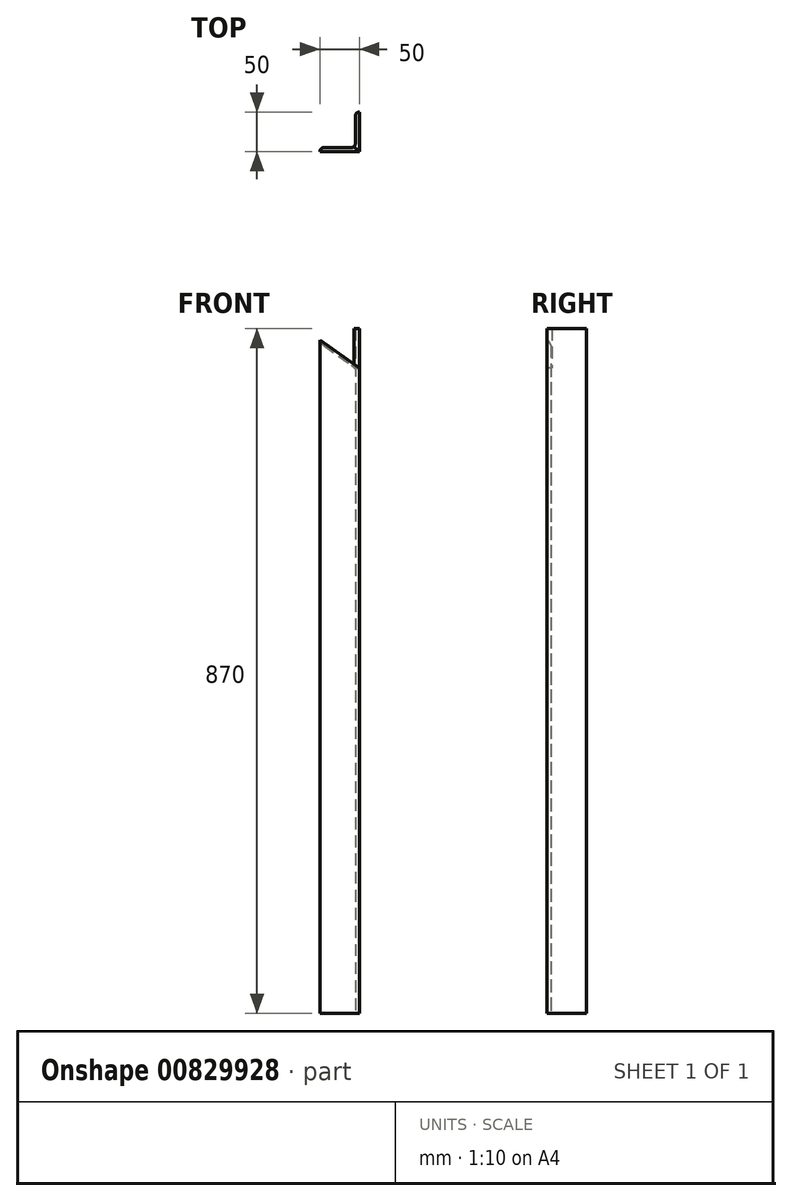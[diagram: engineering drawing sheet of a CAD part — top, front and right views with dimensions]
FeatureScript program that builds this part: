
annotation { "Feature Type Name" : "Feature", "Feature Type Description" : "" }
export const myFeature = defineFeature(function(context is Context, id is Id, definition is map)
    precondition{}
    {
        {
            var Q0;
            Q0=qCreatedBy(makeId("Top.planeOp"),FACE);
            var sketch = newSketch(context, id + "F0", { "sketchPlane" : qUnion([Q0])});
            skLineSegment(sketch, "E0", {"start": v(0, 0) * mm, "end": v(0, 50) * mm});
            skLineSegment(sketch, "E1", {"start": v(0, 0) * mm, "end": v(-50, 0) * mm});
            skLineSegment(sketch, "E2", {"start": v(-50, 0) * mm, "end": v(-50, 0) * mm});
            skLineSegment(sketch, "E3", {"start": v(-45, 5) * mm, "end": v(-10, 5) * mm});
            skLineSegment(sketch, "E4", {"start": v(-5, 10) * mm, "end": v(-5, 45) * mm});
            skLineSegment(sketch, "E5", {"start": v(0, 50) * mm, "end": v(0, 50) * mm});
            skPoint(sketch, "E6.visualSharp", {"position": v(-50, 5) * mm});
            skArc(sketch, "E6.filletArc", {"start": v(-45, 5) * mm, "mid": v(-48.54, 3.54) * mm, "end": v(-50, 0) * mm});
            skPoint(sketch, "E7.visualSharp", {"position": v(-5, 50) * mm});
            skArc(sketch, "E7.filletArc", {"start": v(0, 50) * mm, "mid": v(-3.54, 48.54) * mm, "end": v(-5, 45) * mm});
            skPoint(sketch, "E8.visualSharp", {"position": v(-5, 5) * mm});
            skArc(sketch, "E8.filletArc", {"start": v(-10, 5) * mm, "mid": v(-6.46, 6.46) * mm, "end": v(-5, 10) * mm});
            skSolve(sketch);
        }
        {
            var Q0;
            Q0=makeQuery(id+"F0.imprint","IMPRINT",FACE,{"disambiguationData":[TD([[makeQuery(id+"F0.imprint","IMPRINT",EDGE,{"derivedFrom":sQuery(id+"F0.wireOp",EDGE,"E0")}),1.0]])]});
            extrude(context, id + "F1", {"entities" : qUnion([Q0]), "depth" : (845 + 25) * mm, "offsetDistance" : 25 * mm});
        }
        {
            var Q0;
            Q0=makeQuery(id+"F1.opExtrude","SWEPT_EDGE",EDGE,{"disambiguationData":[OSD([sQuery(id+"F0.wireOp",EDGE,"E0"),sQuery(id+"F0.wireOp",EDGE,"E1")])]});
            cPlane(context, id + "F2", {"entities" : qUnion([Q0]), "cplaneType" : CPlaneType.LINE_ANGLE, "offset" : 25 * mm, "angle" : 45 * degree, "width" : 150 * mm, "height" : 150 * mm});
        }
        {
            var Q0;
            Q0=qCreatedBy(id+"F2.planeOp",FACE);
            var sketch = newSketch(context, id + "F3", { "sketchPlane" : qUnion([Q0])});
            skLineSegment(sketch, "E9", {"start": v(0, 0) * mm, "end": v(0, 870) * mm});
            skLineSegment(sketch, "E10", {"start": v(0, 870) * mm, "end": v(50, 870) * mm});
            skLineSegment(sketch, "E11", {"start": v(0, 870) * mm, "end": v(0, 820) * mm});
            skLineSegment(sketch, "E12", {"start": v(0, 820) * mm, "end": v(50, 870) * mm});
            skLineSegment(sketch, "E13", {"start": v(0, 820) * mm, "end": v(-50, 870) * mm});
            skLineSegment(sketch, "E14", {"start": v(0, 870) * mm, "end": v(-50, 870) * mm});
            skLineSegment(sketch, "E15", {"start": v(0, 0) * mm, "end": v(0, 50) * mm});
            skLineSegment(sketch, "E16", {"start": v(0, 50) * mm, "end": v(-50, 0) * mm});
            skLineSegment(sketch, "E17", {"start": v(0, 0) * mm, "end": v(-50, 0) * mm});
            skLineSegment(sketch, "E18", {"start": v(0, 50) * mm, "end": v(50, 0) * mm});
            skLineSegment(sketch, "E19", {"start": v(50, 0) * mm, "end": v(0, 0) * mm});
            skSolve(sketch);
        }
        {
            var Q0;
            Q0=makeQuery(id+"F3.imprint","IMPRINT",FACE,{"disambiguationData":[TD([[makeQuery(id+"F3.imprint","IMPRINT",EDGE,{"derivedFrom":sQuery(id+"F3.wireOp",EDGE,"E15")}),1.0]])]});
            var Q1;
            Q1=makeQuery(id+"F3.imprint","IMPRINT",FACE,{"disambiguationData":[TD([[makeQuery(id+"F3.imprint","IMPRINT",EDGE,{"derivedFrom":sQuery(id+"F3.wireOp",EDGE,"E15")}),-1.0]])]});
            var Q2;
            Q2=makeQuery(id+"F3.imprint","IMPRINT",FACE,{"disambiguationData":[TD([[makeQuery(id+"F3.imprint","IMPRINT",EDGE,{"derivedFrom":sQuery(id+"F3.wireOp",EDGE,"E11")}),-1.0]])]});
            var Q3;
            Q3=makeQuery(id+"F3.imprint","IMPRINT",FACE,{"disambiguationData":[TD([[makeQuery(id+"F3.imprint","IMPRINT",EDGE,{"derivedFrom":sQuery(id+"F3.wireOp",EDGE,"E10")}),-1.0]])]});
            extrude(context, id + "F4", {"entities" : qUnion([Q0, Q1, Q2, Q3]), "operationType" : NewBodyOperationType.REMOVE, "depth" : 100 * mm, "offsetDistance" : 25 * mm});
        }
    });
